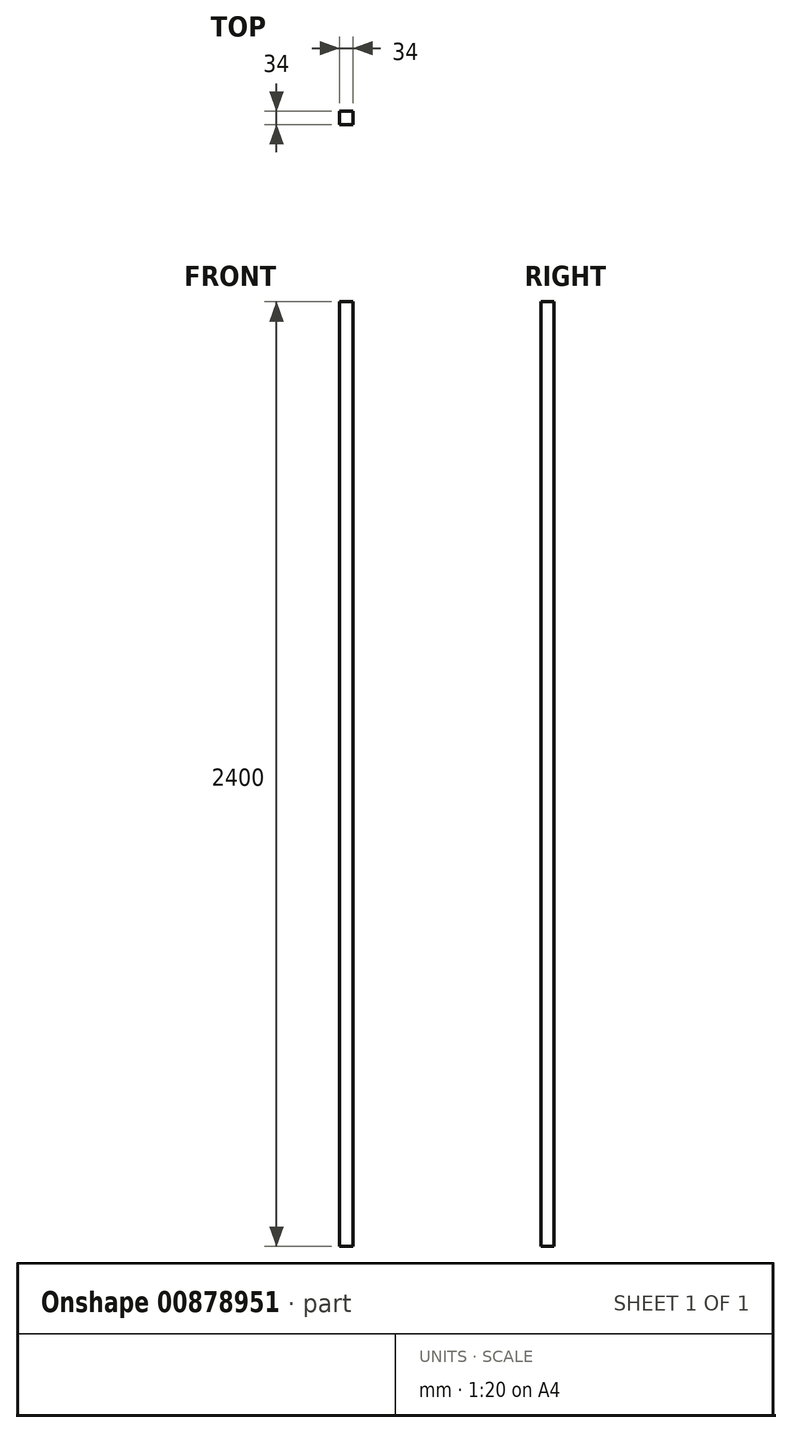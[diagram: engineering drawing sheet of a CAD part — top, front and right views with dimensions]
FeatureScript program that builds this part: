
annotation { "Feature Type Name" : "Feature", "Feature Type Description" : "" }
export const myFeature = defineFeature(function(context is Context, id is Id, definition is map)
    precondition{}
    {
        {
            var Q0;
            Q0=qCreatedBy(makeId("Top.planeOp"),FACE);
            var sketch = newSketch(context, id + "F0", { "sketchPlane" : qUnion([Q0])});
            skLineSegment(sketch, "E0.bottom", {"start": v(17, -17) * mm, "end": v(-17, -17) * mm});
            skLineSegment(sketch, "E0.top", {"start": v(17, 17) * mm, "end": v(-17, 17) * mm});
            skLineSegment(sketch, "E0.left", {"start": v(17, -17) * mm, "end": v(17, 17) * mm});
            skLineSegment(sketch, "E0.right", {"start": v(-17, -17) * mm, "end": v(-17, 17) * mm});
            skPoint(sketch, "E0.middle", {"position": v(0, 0) * mm});
            skSolve(sketch);
        }
        {
            var Q0;
            Q0 = qSketchRegion(id + "F0", true);
            extrude(context, id + "F1", {"entities" : qUnion([Q0]), "depth" : 2400 * mm, "offsetDistance" : 25 * mm});
        }
    });
